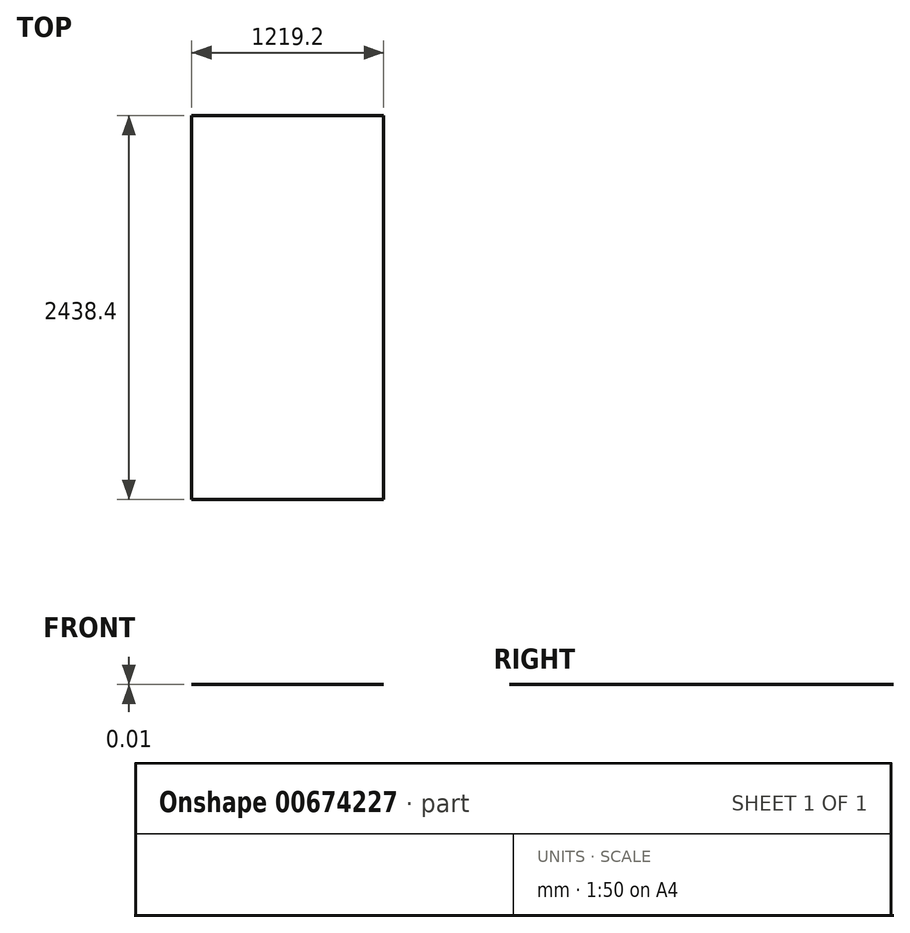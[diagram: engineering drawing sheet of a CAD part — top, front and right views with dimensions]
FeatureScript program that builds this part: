
annotation { "Feature Type Name" : "Feature", "Feature Type Description" : "" }
export const myFeature = defineFeature(function(context is Context, id is Id, definition is map)
    precondition{}
    {
        {
            var Q0;
            Q0=qCreatedBy(makeId("Top.planeOp"),FACE);
            var sketch = newSketch(context, id + "F0", { "sketchPlane" : qUnion([Q0])});
            skLineSegment(sketch, "E0.bottom", {"start": v(-1260.4, 2293.75) * mm, "end": v(-41.2, 2293.75) * mm});
            skLineSegment(sketch, "E0.top", {"start": v(-1260.4, -144.65) * mm, "end": v(-41.2, -144.65) * mm});
            skLineSegment(sketch, "E0.left", {"start": v(-1260.4, 2293.75) * mm, "end": v(-1260.4, -144.65) * mm});
            skLineSegment(sketch, "E0.right", {"start": v(-41.2, 2293.75) * mm, "end": v(-41.2, -144.65) * mm});
            skSolve(sketch);
        }
        {
            var Q0;
            Q0 = qSketchRegion(id + "F0", true);
            extrude(context, id + "F1", {"entities" : qUnion([Q0]), "depth" : 3 / 203.2 * mm, "offsetDistance" : 25 * mm});
        }
    });
